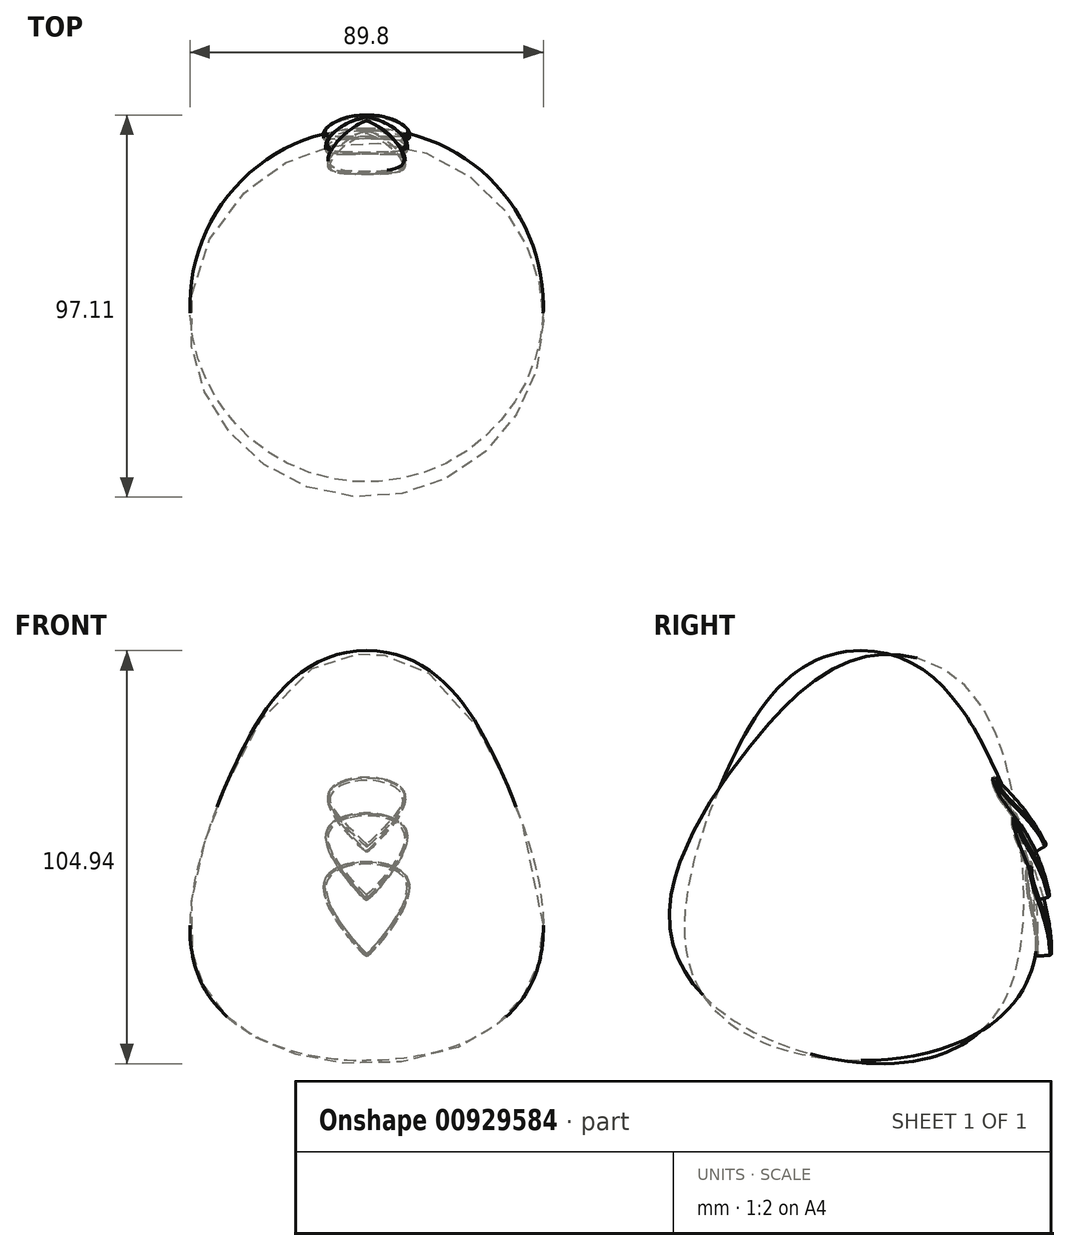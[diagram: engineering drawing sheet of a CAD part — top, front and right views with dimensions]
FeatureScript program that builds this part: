
annotation { "Feature Type Name" : "Feature", "Feature Type Description" : "" }
export const myFeature = defineFeature(function(context is Context, id is Id, definition is map)
    precondition{}
    {
        {
            var Q0;
            Q0=qCreatedBy(makeId("Front.planeOp"),FACE);
            var sketch = newSketch(context, id + "F0", { "sketchPlane" : qUnion([Q0])});
            skFitSpline(sketch, "E0", {"points": [v(0, 54.53) * mm, v(34.66, 22.84) * mm, v(42.6, -28.45) * mm, v(0, -49.62) * mm], "startDerivative": vector(163.32, -1.13) * mm, "endDerivative": vector(-193.06, -1.18) * mm});
            skLineSegment(sketch, "E1", {"start": v(0, 58.92) * mm, "end": v(0, -63.18) * mm});
            skLineSegment(sketch, "E2", {"start": v(-35.5, 0) * mm, "end": v(29.07, 0) * mm});
            skLineSegment(sketch, "E3", {"start": v(28.57, 10.2) * mm, "end": v(-32.3, 10.2) * mm});
            skLineSegment(sketch, "E4", {"start": v(-29.12, 20.9) * mm, "end": v(23.72, 20.9) * mm});
            skLineSegment(sketch, "E5", {"start": v(20.04, 31.43) * mm, "end": v(-26.1, 31.43) * mm});
            skLineSegment(sketch, "E6", {"start": v(14.86, 41.97) * mm, "end": v(-22.1, 41.97) * mm});
            skLineSegment(sketch, "E7", {"start": v(29.4, -10.53) * mm, "end": v(-32.3, -10.53) * mm});
            skLineSegment(sketch, "E8", {"start": v(-31.63, -21.57) * mm, "end": v(27.56, -21.57) * mm});
            skLineSegment(sketch, "E9", {"start": v(27.4, -30.1) * mm, "end": v(-28.62, -30.1) * mm});
            skLineSegment(sketch, "E10", {"start": v(-23.6, -38.8) * mm, "end": v(22.04, -38.8) * mm});
            skSolve(sketch);
        }
        {
            var Q0;
            {var subQ0=sQuery(id+"F0.wireOp",EDGE,"E0");Q0=makeQuery(id+"F0.imprint","IMPRINT",FACE,{"disambiguationData":[TD([[makeQuery(id+"F0.imprint","IMPRINT",EDGE,{"derivedFrom":subQ0}),-1.0]])]});}
            var Q1;
            Q1=sQuery(id+"F0.wireOp",EDGE,"E0");
            var Q2;
            Q2=sQuery(id+"F0.wireOp",EDGE,"E1");
            revolve(context, id + "F1", {"surfaceOperationType" : NewSurfaceOperationType.NEW, "entities" : qUnion([Q0]), "surfaceEntities" : qUnion([Q1]), "axis" : qUnion([Q2]), "revolveType" : RevolveType.FULL});
        }
        {
            var Q0;
            Q0=makeQuery(id+"F1.opRevolve","SWEPT_BODY",BODY,{"disambiguationData":[OSD([sQuery(id+"F0.wireOp",EDGE,"E0")])]});
            var Q1;
            Q1=sQuery(id+"F0.wireOp",EDGE,"E2");
            transform(context, id + "F2", {"entities" : qUnion([Q0]), "transformType" : TransformType.ROTATION, "transformAxis" : qUnion([Q1]), "angle" : 15 * degree, "oppositeDirection" : true, "makeCopy" : true});
        }
        {
            var Q0;
            Q0=qCreatedBy(makeId("Front.planeOp"),FACE);
            var sketch = newSketch(context, id + "F3", { "sketchPlane" : qUnion([Q0])});
            skFitSpline(sketch, "E11", {"points": [v(-10.42, 0) * mm, v(10.37, 0) * mm, v(0.7, -19.5) * mm, v(-0.67, -19.5) * mm, v(-10.42, 0) * mm]});
            skSolve(sketch);
        }
        {
            var Q0;
            Q0=makeQuery(id+"F3.imprint","IMPRINT",FACE,{"disambiguationData":[TD([[makeQuery(id+"F3.imprint","IMPRINT",EDGE,{"derivedFrom":sQuery(id+"F3.wireOp",EDGE,"E11")}),-1.0]])]});
            var Q1;
            Q1=makeQuery(id+"F1.opRevolve","SWEPT_FACE",FACE,{"disambiguationData":[OSD([sQuery(id+"F0.wireOp",EDGE,"E0")])]});
            var Q2;
            Q2=makeQuery(id+"F2.opPattern","COPY",FACE,{"derivedFrom":makeQuery(id+"F1.opRevolve","SWEPT_FACE",FACE,{"disambiguationData":[OSD([sQuery(id+"F0.wireOp",EDGE,"E0")])]}),"instanceName":"1"});
            extrude(context, id + "F4", {"entities" : qUnion([Q0]), "endBound" : BoundingType.UP_TO_SURFACE, "oppositeDirection" : true, "depth" : 25 * mm, "endBoundEntityFace" : qUnion([Q1]), "offsetDistance" : 25 * mm, "hasSecondDirection" : true, "secondDirectionBound" : SecondDirectionBoundingType.UP_TO_SURFACE, "secondDirectionOppositeDirection" : true, "secondDirectionDepth" : 25 * mm, "secondDirectionBoundEntityFace" : qUnion([Q2])});
        }
        {
            var Q0;
            Q0=makeQuery(id+"F4.opExtrude","CAP_EDGE",EDGE,{"disambiguationData":[OSD([sQuery(id+"F3.wireOp",EDGE,"E11")]),topologyDisambiguationEdgeConnected([makeQuery(id+"F1.opRevolve","SWEPT_FACE",FACE,{"disambiguationData":[OSD([sQuery(id+"F0.wireOp",EDGE,"E0")])]})])],"isStart":false});
            var Q1;
            Q1=makeQuery(id+"F4.opExtrude","CAP_EDGE",EDGE,{"disambiguationData":[OSD([sQuery(id+"F3.wireOp",EDGE,"E11")]),topologyDisambiguationEdgeConnected([makeQuery(id+"F2.opPattern","COPY",FACE,{"derivedFrom":makeQuery(id+"F1.opRevolve","SWEPT_FACE",FACE,{"disambiguationData":[OSD([sQuery(id+"F0.wireOp",EDGE,"E0")])]}),"instanceName":"1"})])],"isStart":false});
            fillet(context, id + "F5", {"entities" : qUnion([Q0, Q1]), "radius" : .5 * mm, "tangentPropagation" : true, "allowEdgeOverflow" : false});
        }
        {
            var Q0;
            Q0=makeQuery(id+"F4.opExtrude","SWEPT_BODY",BODY,{"disambiguationData":[OSD([sQuery(id+"F3.wireOp",EDGE,"E11")])]});
            var Q1;
            Q1=sQuery(id+"F0.wireOp",EDGE,"E7");
            transform(context, id + "F6", {"entities" : qUnion([Q0]), "transformType" : TransformType.ROTATION, "transformAxis" : qUnion([Q1]), "angle" : 15 * degree, "oppositeDirection" : true, "makeCopy" : true});
        }
        {
            var Q0;
            Q0=makeQuery(id+"F6.opPattern","COPY",BODY,{"derivedFrom":makeQuery(id+"F4.opExtrude","SWEPT_BODY",BODY,{"disambiguationData":[OSD([sQuery(id+"F3.wireOp",EDGE,"E11")])]}),"instanceName":"1"});
            transform(context, id + "F7", {"entities" : qUnion([Q0]), "transformType" : TransformType.TRANSLATION_3D, "dx" : 0 * mm, "dy" : 2.3 * mm, "dz" : 0 * mm, "makeCopy" : false});
        }
        {
            var Q0;
            Q0=makeQuery(id+"F6.opPattern","COPY",BODY,{"derivedFrom":makeQuery(id+"F4.opExtrude","SWEPT_BODY",BODY,{"disambiguationData":[OSD([sQuery(id+"F3.wireOp",EDGE,"E11")])]}),"instanceName":"1"});
            var Q1;
            {var subQ0=makeQuery(id+"F1.opRevolve","SWEPT_FACE",FACE,{"disambiguationData":[OSD([sQuery(id+"F0.wireOp",EDGE,"E0")])]});var subQ1=sQuery(id+"F3.wireOp",EDGE,"E11");Q1=makeQuery(id+"F6.opPattern","COPY",VERTEX,{"derivedFrom":makeQuery(id+"F5.opFillet","BLEND_VERTEX",VERTEX,{"disambiguationData":[OD(1.0)],"blendedFrom":[makeQuery(id+"F4.opExtrude","CAP_EDGE",EDGE,{"disambiguationData":[OSD([subQ1]),topologyDisambiguationEdgeConnected([subQ0])],"isStart":false}),makeQuery(id+"F4.opExtrude","CAP_FACE",FACE,{"disambiguationData":[OSD([subQ1]),topologyDisambiguationEdgeConnected([subQ0])],"isStart":false})],"blendedInto":[makeQuery(id+"F4.opExtrude","CAP_FACE",FACE,{"disambiguationData":[OSD([subQ1]),topologyDisambiguationEdgeConnected([subQ0])],"isStart":false})]}),"instanceName":"1"});}
            transform(context, id + "F8", {"entities" : qUnion([Q0]), "transformType" : TransformType.SCALE_UNIFORMLY, "scale" : .95, "scalePoint" : qUnion([Q1]), "makeCopy" : false});
        }
        {
            var Q0;
            Q0=makeQuery(id+"F6.opPattern","COPY",BODY,{"derivedFrom":makeQuery(id+"F4.opExtrude","SWEPT_BODY",BODY,{"disambiguationData":[OSD([sQuery(id+"F3.wireOp",EDGE,"E11")])]}),"instanceName":"1"});
            var Q1;
            Q1=sQuery(id+"F0.wireOp",EDGE,"E2");
            var Q2;
            Q2=sQuery(id+"F0.wireOp",EDGE,"E3");
            transform(context, id + "F9", {"entities" : qUnion([Q0]), "transformType" : TransformType.ROTATION, "transformAxis" : qUnion([Q2]), "angle" : 15 * degree, "oppositeDirection" : true, "makeCopy" : true});
        }
        {
            var Q0;
            Q0=makeQuery(id+"F9.opPattern","COPY",BODY,{"derivedFrom":makeQuery(id+"F6.opPattern","COPY",BODY,{"derivedFrom":makeQuery(id+"F4.opExtrude","SWEPT_BODY",BODY,{"disambiguationData":[OSD([sQuery(id+"F3.wireOp",EDGE,"E11")])]}),"instanceName":"1"}),"instanceName":"1"});
            transform(context, id + "F10", {"entities" : qUnion([Q0]), "transformType" : TransformType.TRANSLATION_3D, "dx" : 0 * mm, "dy" : -3.9 * mm, "dz" : 0 * mm, "makeCopy" : false});
        }
        {
            var Q0;
            Q0=makeQuery(id+"F9.opPattern","COPY",BODY,{"derivedFrom":makeQuery(id+"F6.opPattern","COPY",BODY,{"derivedFrom":makeQuery(id+"F4.opExtrude","SWEPT_BODY",BODY,{"disambiguationData":[OSD([sQuery(id+"F3.wireOp",EDGE,"E11")])]}),"instanceName":"1"}),"instanceName":"1"});
            var Q1;
            {var subQ0=makeQuery(id+"F1.opRevolve","SWEPT_FACE",FACE,{"disambiguationData":[OSD([sQuery(id+"F0.wireOp",EDGE,"E0")])]});var subQ1=sQuery(id+"F3.wireOp",EDGE,"E11");Q1=makeQuery(id+"F9.opPattern","COPY",VERTEX,{"derivedFrom":makeQuery(id+"F6.opPattern","COPY",VERTEX,{"derivedFrom":makeQuery(id+"F5.opFillet","BLEND_VERTEX",VERTEX,{"disambiguationData":[OD(1.0)],"blendedFrom":[makeQuery(id+"F4.opExtrude","CAP_EDGE",EDGE,{"disambiguationData":[OSD([subQ1]),topologyDisambiguationEdgeConnected([subQ0])],"isStart":false}),makeQuery(id+"F4.opExtrude","CAP_FACE",FACE,{"disambiguationData":[OSD([subQ1]),topologyDisambiguationEdgeConnected([subQ0])],"isStart":false})],"blendedInto":[makeQuery(id+"F4.opExtrude","CAP_FACE",FACE,{"disambiguationData":[OSD([subQ1]),topologyDisambiguationEdgeConnected([subQ0])],"isStart":false})]}),"instanceName":"1"}),"instanceName":"1"});}
            transform(context, id + "F11", {"entities" : qUnion([Q0]), "transformType" : TransformType.SCALE_UNIFORMLY, "scale" : .95, "scalePoint" : qUnion([Q1]), "makeCopy" : false});
        }
        {
            var Q0;
            Q0=makeQuery(id+"F4.opExtrude","SWEPT_BODY",BODY,{"disambiguationData":[OSD([sQuery(id+"F3.wireOp",EDGE,"E11")])]});
            var Q1;
            Q1=sQuery(id+"F0.wireOp",EDGE,"E10");
            transform(context, id + "F12", {"entities" : qUnion([Q0]), "transformType" : TransformType.ROTATION, "transformAxis" : qUnion([Q1]), "angle" : 5 * degree, "makeCopy" : false});
        }
        {
            var Q0;
            Q0=makeQuery(id+"F4.opExtrude","SWEPT_BODY",BODY,{"disambiguationData":[OSD([sQuery(id+"F3.wireOp",EDGE,"E11")])]});
            transform(context, id + "F13", {"entities" : qUnion([Q0]), "transformType" : TransformType.TRANSLATION_3D, "dx" : 0 * mm, "dy" : 5.5 * mm, "dz" : -6.7 * mm, "makeCopy" : false});
        }
    });
